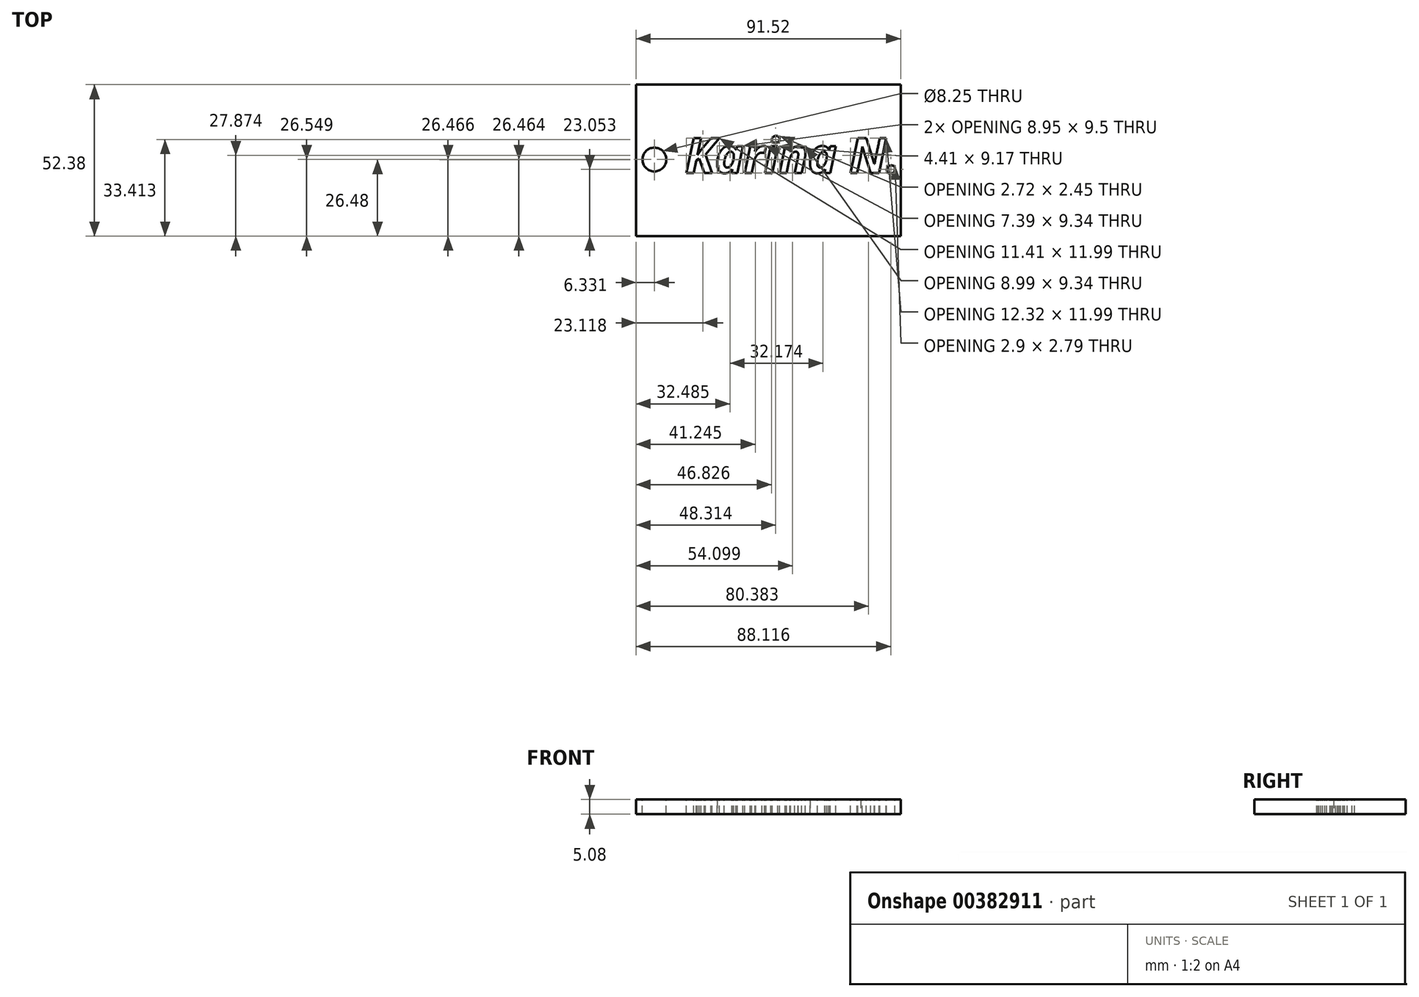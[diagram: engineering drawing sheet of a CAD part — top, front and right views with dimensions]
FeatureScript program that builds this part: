
annotation { "Feature Type Name" : "Feature", "Feature Type Description" : "" }
export const myFeature = defineFeature(function(context is Context, id is Id, definition is map)
    precondition{}
    {
        {
            var Q0;
            Q0=qCreatedBy(makeId("Top.planeOp"),FACE);
            var sketch = newSketch(context, id + "F0", { "sketchPlane" : qUnion([Q0])});
            skLineSegment(sketch, "E0.bottom", {"start": v(-28.78, 25.9) * mm, "end": v(62.74, 25.9) * mm});
            skLineSegment(sketch, "E0.top", {"start": v(-28.78, -26.48) * mm, "end": v(62.74, -26.48) * mm});
            skLineSegment(sketch, "E0.left", {"start": v(-28.78, 25.9) * mm, "end": v(-28.78, -26.48) * mm});
            skLineSegment(sketch, "E0.right", {"start": v(62.74, 25.9) * mm, "end": v(62.74, -26.48) * mm});
            skSolve(sketch);
        }
        {
            var Q0;
            Q0=makeQuery(id+"F0.imprint","IMPRINT",FACE,{"disambiguationData":[TD([[makeQuery(id+"F0.imprint","IMPRINT",EDGE,{"derivedFrom":sQuery(id+"F0.wireOp",EDGE,"E0.bottom")}),-1.0]])]});
            extrude(context, id + "F1", {"entities" : qUnion([Q0]), "depth" : 5.08 * mm});
        }
        {
            var Q0;
            Q0=makeQuery(id+"F1.opExtrude","CAP_FACE",FACE,{"disambiguationData":[OSD([sQuery(id+"F0.wireOp",EDGE,"E0.bottom"),sQuery(id+"F0.wireOp",EDGE,"E0.top"),sQuery(id+"F0.wireOp",EDGE,"E0.left"),sQuery(id+"F0.wireOp",EDGE,"E0.right")])],"isStart":false});
            var sketch = newSketch(context, id + "F2", { "sketchPlane" : qUnion([Q0])});
            skCircle(sketch, "E1", {"center": v(-22.45, 0) * mm, "radius": 4.13 * mm});
            skText(sketch, "E2", { "text": "Karina N.", "fontName": "OpenSans-BoldItalic.ttf"});
            const initialGuessF2  = {"E2": [-0.0118, -0.0046, 1, 0, 0.01209]};
            skSetInitialGuess(sketch, initialGuessF2);
            skSolve(sketch);
        }
        {
            var Q0;
            Q0 = qSketchRegion(id + "F2", true);
            extrude(context, id + "F3", {"entities" : qUnion([Q0]), "operationType" : NewBodyOperationType.REMOVE, "oppositeDirection" : true, "depth" : 25.4 * mm});
        }
    });
